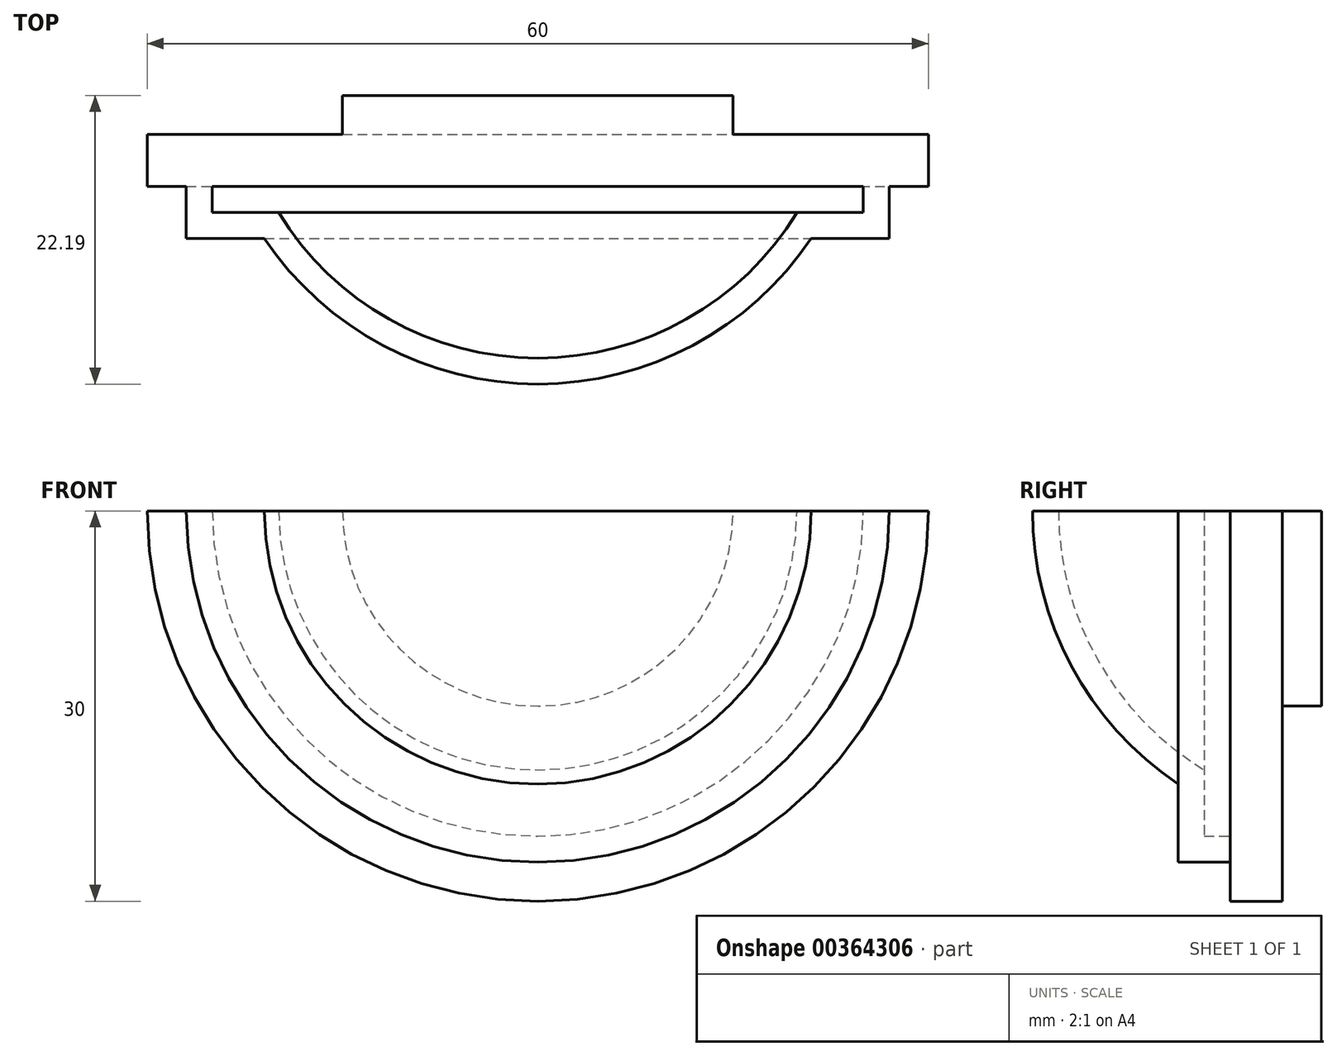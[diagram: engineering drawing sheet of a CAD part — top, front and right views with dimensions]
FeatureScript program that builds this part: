
annotation { "Feature Type Name" : "Feature", "Feature Type Description" : "" }
export const myFeature = defineFeature(function(context is Context, id is Id, definition is map)
    precondition{}
    {
        {
            var Q0;
            Q0=qCreatedBy(makeId("Front.planeOp"),FACE);
            var sketch = newSketch(context, id + "F0", { "sketchPlane" : qUnion([Q0])});
            skArc(sketch, "E0", {"start": v(-15, 0) * mm, "mid": v(0, -15) * mm, "end": v(15, 0) * mm});
            skArc(sketch, "E1", {"start": v(30, 0) * mm, "mid": v(0, -30) * mm, "end": v(-30, 0) * mm});
            skLineSegment(sketch, "E2", {"start": v(-30, 0) * mm, "end": v(30, 0) * mm});
            skSolve(sketch);
        }
        {
            var Q0;
            {var subQ0=sQuery(id+"F0.wireOp",EDGE,"E0");Q0=makeQuery(id+"F0.imprint","IMPRINT",FACE,{"disambiguationData":[TD([[makeQuery(id+"F0.imprint","IMPRINT",EDGE,{"derivedFrom":subQ0}),1.0]])]});}
            extrude(context, id + "F1", {"entities" : qUnion([Q0]), "oppositeDirection" : true, "depth" : 3 * mm, "offsetDistance" : 25 * mm});
        }
        {
            var Q0;
            {var subQ0=sQuery(id+"F0.wireOp",EDGE,"E0");Q0=makeQuery(id+"F0.imprint","IMPRINT",FACE,{"disambiguationData":[TD([[makeQuery(id+"F0.imprint","IMPRINT",EDGE,{"derivedFrom":subQ0}),-1.0]])]});}
            var Q1;
            {var subQ0=sQuery(id+"F0.wireOp",EDGE,"E0");Q1=makeQuery(id+"F0.imprint","IMPRINT",FACE,{"disambiguationData":[TD([[makeQuery(id+"F0.imprint","IMPRINT",EDGE,{"derivedFrom":subQ0}),1.0]])]});}
            extrude(context, id + "F2", {"entities" : qUnion([Q0, Q1]), "operationType" : NewBodyOperationType.ADD, "depth" : 2 * mm, "offsetDistance" : 25 * mm});
        }
        {
            var Q0;
            Q0=makeQuery(id+"F2.opExtrude","CAP_FACE",FACE,{"disambiguationData":[OSD([sQuery(id+"F0.wireOp",EDGE,"E1"),sQuery(id+"F0.wireOp",EDGE,"E2")])],"isStart":false});
            var sketch = newSketch(context, id + "F3", { "sketchPlane" : qUnion([Q0])});
            skArc(sketch, "E3", {"start": v(27, 0) * mm, "mid": v(0, -27) * mm, "end": v(-27, 0) * mm});
            skArc(sketch, "E4", {"start": v(24, 0) * mm, "mid": v(0, -24) * mm, "end": v(-24, 0) * mm});
            skSolve(sketch);
        }
        {
            var Q0;
            {var subQ0=sQuery(id+"F3.wireOp",EDGE,"E3");Q0=makeQuery(id+"F3.imprint","IMPRINT",FACE,{"disambiguationData":[TD([[makeQuery(id+"F3.imprint","IMPRINT",EDGE,{"derivedFrom":subQ0}),-1.0]])]});}
            extrude(context, id + "F4", {"entities" : qUnion([Q0]), "operationType" : NewBodyOperationType.ADD, "depth" : 2 * mm, "offsetDistance" : 25 * mm});
        }
        {
            var Q0;
            {var subQ1=sQuery(id+"F0.wireOp",EDGE,"E2");var subQ3=sQuery(id+"F3.wireOp",EDGE,"E4");Q0=makeQuery(id+"F4.boolean.opBoolean","SPLIT",FACE,{"disambiguationData":[TD([makeQuery(id+"F4.opExtrude","SWEPT_FACE",FACE,{"disambiguationData":[OSD([subQ3])]})])],"derivedFrom":makeQuery(id+"F2.opExtrude","CAP_FACE",FACE,{"disambiguationData":[OSD([sQuery(id+"F0.wireOp",EDGE,"E1"),subQ1])],"isStart":false})});}
            extrude(context, id + "F5", {"entities" : qUnion([Q0]), "operationType" : NewBodyOperationType.ADD, "depth" : 4 * mm, "offsetDistance" : 25 * mm});
        }
        {
            var Q0;
            Q0=makeQuery(id+"F5.opExtrude","CAP_FACE",FACE,{"disambiguationData":[OSD([sQuery(id+"F0.wireOp",EDGE,"E1"),sQuery(id+"F0.wireOp",EDGE,"E2")])],"isStart":false});
            var sketch = newSketch(context, id + "F6", { "sketchPlane" : qUnion([Q0])});
            skArc(sketch, "E5.0", {"start": v(21, 0) * mm, "mid": v(0, -21) * mm, "end": v(-21, 0) * mm});
            skSolve(sketch);
        }
        {
            var Q0;
            {var subQ0=sQuery(id+"F6.wireOp",EDGE,"E5.0");Q0=makeQuery(id+"F6.imprint","IMPRINT",FACE,{"disambiguationData":[TD([[makeQuery(id+"F6.imprint","IMPRINT",EDGE,{"derivedFrom":subQ0}),-1.0]])]});}
            extrude(context, id + "F7", {"entities" : qUnion([Q0]), "operationType" : NewBodyOperationType.ADD, "depth" : 2 * mm, "offsetDistance" : 25 * mm});
        }
        {
            var Q0;
            {var subQ0=sQuery(id+"F0.wireOp",EDGE,"E2");var subQ1=sQuery(id+"F3.wireOp",EDGE,"E3");var subQ2=makeQuery(id+"F2.opExtrude","CAP_EDGE",EDGE,{"disambiguationData":[OSD([subQ0])],"isStart":false});Q0=makeQuery(id+"F7.boolean.opBoolean","MERGE",FACE,{"derivedFrom":[makeQuery(id+"F5.boolean.opBoolean","MERGE",FACE,{"derivedFrom":[makeQuery(id+"F4.boolean.opBoolean","MERGE",FACE,{"derivedFrom":[makeQuery(id+"F2.boolean.opBoolean","MERGE",FACE,{"derivedFrom":[makeQuery(id+"F1.opExtrude","SWEPT_FACE",FACE,{"disambiguationData":[OSD([subQ0])]}),makeQuery(id+"F2.opExtrude","SWEPT_FACE",FACE,{"disambiguationData":[OSD([subQ0])]})]}),makeQuery(id+"F4.opExtrude","SWEPT_FACE",FACE,{"disambiguationData":[OSD([subQ0]),TDD([makeQuery(id+"F3.imprint","IMPRINT",EDGE,{"disambiguationData":[TD([[makeQuery(id+"F3.imprint","INTERSECT",VERTEX,{"disambiguationData":[OD(0.0)],"derivedFrom":[subQ2,subQ1]}),1.0]])],"derivedFrom":subQ2})])]}),makeQuery(id+"F4.opExtrude","SWEPT_FACE",FACE,{"disambiguationData":[OSD([subQ0]),TDD([makeQuery(id+"F3.imprint","IMPRINT",EDGE,{"disambiguationData":[TD([[makeQuery(id+"F3.imprint","INTERSECT",VERTEX,{"disambiguationData":[OD(1.0)],"derivedFrom":[subQ2,subQ1]}),-1.0]])],"derivedFrom":subQ2})])]})]}),makeQuery(id+"F5.opExtrude","SWEPT_FACE",FACE,{"disambiguationData":[OSD([subQ0])]})]}),makeQuery(id+"F7.opExtrude","SWEPT_FACE",FACE,{"disambiguationData":[OSD([subQ0])]})]});}
            var sketch = newSketch(context, id + "F8", { "sketchPlane" : qUnion([Q0])});
            skArc(sketch, "E6", {"start": v(-21, -8) * mm, "mid": v(0, -19.19) * mm, "end": v(21, -8) * mm});
            skLineSegment(sketch, "E7", {"start": v(0, 19.77) * mm, "end": v(0, -19.19) * mm});
            skSolve(sketch);
        }
        {
            var Q0;
            {var subQ0=sQuery(id+"F8.wireOp",EDGE,"E6");var subQ5=sQuery(id+"F8.wireOp",EDGE,"E7");var subQ6=makeQuery(id+"F8.imprint","INTERSECT",VERTEX,{"derivedFrom":[subQ0,subQ5]});Q0=makeQuery(id+"F8.imprint","IMPRINT",FACE,{"disambiguationData":[TD([[makeQuery(id+"F8.imprint","IMPRINT",EDGE,{"disambiguationData":[TD([[subQ6,1.0]])],"derivedFrom":subQ5}),-1.0]])]});}
            var Q1;
            Q1=sQuery(id+"F8.wireOp",EDGE,"E7");
            revolve(context, id + "F9", {"operationType" : NewBodyOperationType.ADD, "surfaceOperationType" : NewSurfaceOperationType.NEW, "entities" : qUnion([Q0]), "axis" : qUnion([Q1]), "revolveType" : RevolveType.ONE_DIRECTION, "angle" : 180 * degree});
        }
        {
            var Q0;
            {var subQ0=sQuery(id+"F0.wireOp",EDGE,"E2");var subQ1=sQuery(id+"F3.wireOp",EDGE,"E3");var subQ2=makeQuery(id+"F2.opExtrude","CAP_EDGE",EDGE,{"disambiguationData":[OSD([subQ0])],"isStart":false});Q0=makeQuery(id+"F9.boolean.opBoolean","MERGE",FACE,{"derivedFrom":[makeQuery(id+"F7.boolean.opBoolean","MERGE",FACE,{"derivedFrom":[makeQuery(id+"F5.boolean.opBoolean","MERGE",FACE,{"derivedFrom":[makeQuery(id+"F4.boolean.opBoolean","MERGE",FACE,{"derivedFrom":[makeQuery(id+"F2.boolean.opBoolean","MERGE",FACE,{"derivedFrom":[makeQuery(id+"F1.opExtrude","SWEPT_FACE",FACE,{"disambiguationData":[OSD([subQ0])]}),makeQuery(id+"F2.opExtrude","SWEPT_FACE",FACE,{"disambiguationData":[OSD([subQ0])]})]}),makeQuery(id+"F4.opExtrude","SWEPT_FACE",FACE,{"disambiguationData":[OSD([subQ0]),TDD([makeQuery(id+"F3.imprint","IMPRINT",EDGE,{"disambiguationData":[TD([[makeQuery(id+"F3.imprint","INTERSECT",VERTEX,{"disambiguationData":[OD(0.0)],"derivedFrom":[subQ2,subQ1]}),1.0]])],"derivedFrom":subQ2})])]}),makeQuery(id+"F4.opExtrude","SWEPT_FACE",FACE,{"disambiguationData":[OSD([subQ0]),TDD([makeQuery(id+"F3.imprint","IMPRINT",EDGE,{"disambiguationData":[TD([[makeQuery(id+"F3.imprint","INTERSECT",VERTEX,{"disambiguationData":[OD(1.0)],"derivedFrom":[subQ2,subQ1]}),-1.0]])],"derivedFrom":subQ2})])]})]}),makeQuery(id+"F5.opExtrude","SWEPT_FACE",FACE,{"disambiguationData":[OSD([subQ0])]})]}),makeQuery(id+"F7.opExtrude","SWEPT_FACE",FACE,{"disambiguationData":[OSD([subQ0])]})]}),makeQuery(id+"F9.opRevolve","CAP_FACE",FACE,{"disambiguationData":[OSD([subQ0,sQuery(id+"F8.wireOp",EDGE,"E6"),sQuery(id+"F8.wireOp",EDGE,"E7")])],"isStart":true})]});}
            shell(context, id + "F10", {"entities" : qUnion([Q0]), "thickness" : 2 * mm});
        }
        {
            var Q0;
            Q0=makeQuery(id+"F10.opShell","OFFSET_FACE",FACE,{"disambiguationData":[OSD([sQuery(id+"F0.wireOp",EDGE,"E0"),sQuery(id+"F0.wireOp",EDGE,"E2")])]});
            var Q1;
            Q1=makeQuery(id+"F10.opShell","OFFSET_FACE",FACE,{"disambiguationData":[OSD([sQuery(id+"F0.wireOp",EDGE,"E1"),sQuery(id+"F0.wireOp",EDGE,"E2")])]});
            extrude(context, id + "F11", {"entities" : qUnion([Q0]), "operationType" : NewBodyOperationType.ADD, "endBound" : BoundingType.UP_TO_SURFACE, "depth" : 25 * mm, "endBoundEntityFace" : qUnion([Q1]), "offsetDistance" : 25 * mm});
        }
        {
            var Q0;
            Q0=makeQuery(id+"F11.opExtrude","CAP_FACE",FACE,{"disambiguationData":[OSD([sQuery(id+"F0.wireOp",EDGE,"E1"),sQuery(id+"F0.wireOp",EDGE,"E2")])],"isStart":false});
            extrude(context, id + "F12", {"entities" : qUnion([Q0]), "operationType" : NewBodyOperationType.REMOVE, "oppositeDirection" : true, "depth" : 1 * mm, "offsetDistance" : 25 * mm});
        }
        {
            var Q0;
            Q0=makeQuery(id+"F12.boolean.opBoolean","COPY",FACE,{"derivedFrom":makeQuery(id+"F12.opExtrude","CAP_FACE",FACE,{"disambiguationData":[OSD([sQuery(id+"F0.wireOp",EDGE,"E1"),sQuery(id+"F0.wireOp",EDGE,"E2")])],"isStart":false})});
            extrude(context, id + "F13", {"entities" : qUnion([Q0]), "operationType" : NewBodyOperationType.ADD, "depth" : 3 * mm, "offsetDistance" : 25 * mm});
        }
    });
